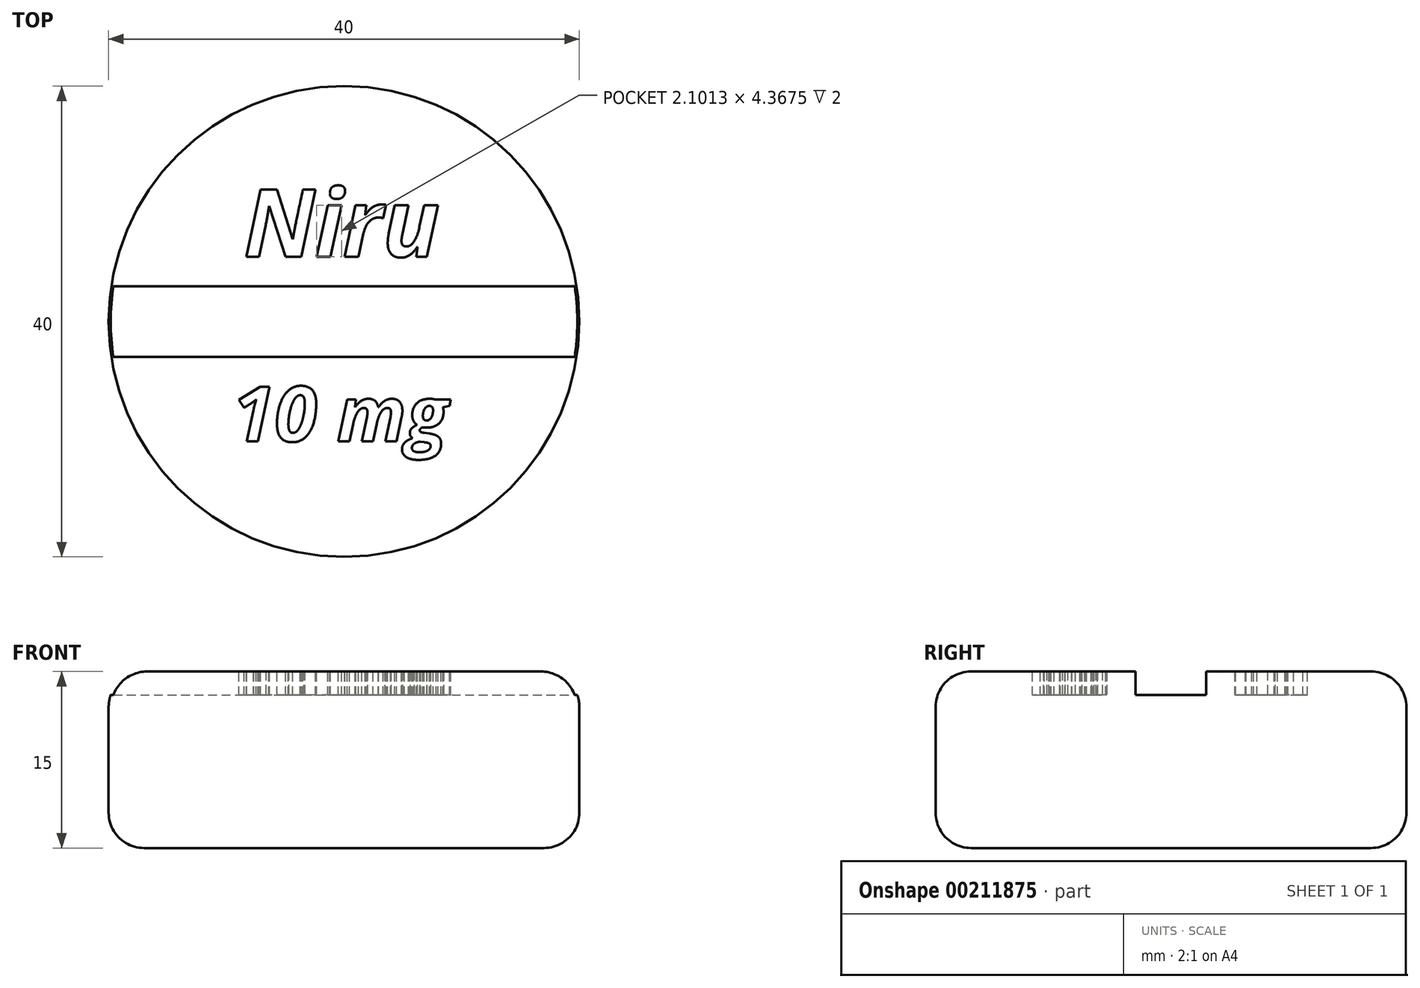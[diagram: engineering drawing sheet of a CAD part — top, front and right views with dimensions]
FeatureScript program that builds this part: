
annotation { "Feature Type Name" : "Feature", "Feature Type Description" : "" }
export const myFeature = defineFeature(function(context is Context, id is Id, definition is map)
    precondition{}
    {
        {
            var Q0;
            Q0=qCreatedBy(makeId("Top.planeOp"),FACE);
            var sketch = newSketch(context, id + "F0", { "sketchPlane" : qUnion([Q0])});
            skCircle(sketch, "E0", {"center": v(0, 0) * mm, "radius": 20 * mm});
            skSolve(sketch);
        }
        {
            var Q0;
            Q0=makeQuery(id+"F0.imprint","IMPRINT",FACE,{"disambiguationData":[TD([[makeQuery(id+"F0.imprint","IMPRINT",EDGE,{"derivedFrom":sQuery(id+"F0.wireOp",EDGE,"E0")}),1.0]])]});
            extrude(context, id + "F1", {"entities" : qUnion([Q0]), "depth" : 15 * mm});
        }
        {
            var Q0;
            Q0=makeQuery(id+"F1.opExtrude","CAP_EDGE",EDGE,{"disambiguationData":[OSD([sQuery(id+"F0.wireOp",EDGE,"E0")])],"isStart":false});
            var Q1;
            Q1=makeQuery(id+"F1.opExtrude","CAP_EDGE",EDGE,{"disambiguationData":[OSD([sQuery(id+"F0.wireOp",EDGE,"E0")])],"isStart":true});
            fillet(context, id + "F2", {"entities" : qUnion([Q0, Q1]), "radius" : 3 * mm, "tangentPropagation" : true, "allowEdgeOverflow" : false});
        }
        {
            var Q0;
            Q0=makeQuery(id+"F1.opExtrude","CAP_FACE",FACE,{"disambiguationData":[OSD([sQuery(id+"F0.wireOp",EDGE,"E0")])],"isStart":false});
            var sketch = newSketch(context, id + "F3", { "sketchPlane" : qUnion([Q0])});
            skLineSegment(sketch, "E1.bottom", {"start": v(-20, 3) * mm, "end": v(20, 3) * mm});
            skLineSegment(sketch, "E1.top", {"start": v(-20, -3) * mm, "end": v(20, -3) * mm});
            skLineSegment(sketch, "E1.left", {"start": v(-20, 3) * mm, "end": v(-20, -3) * mm});
            skLineSegment(sketch, "E1.right", {"start": v(20, 3) * mm, "end": v(20, -3) * mm});
            skSolve(sketch);
        }
        {
            var Q0;
            Q0 = qSketchRegion(id + "F3", true);
            extrude(context, id + "F4", {"entities" : qUnion([Q0]), "operationType" : NewBodyOperationType.REMOVE, "oppositeDirection" : true, "depth" : 2 * mm});
        }
        {
            var Q0;
            {var subQ0=sQuery(id+"F0.wireOp",EDGE,"E0");Q0=makeQuery(id+"F4.boolean.opBoolean","SPLIT",FACE,{"disambiguationData":[TD([makeQuery(id+"F4.opExtrude","SWEPT_FACE",FACE,{"disambiguationData":[OSD([sQuery(id+"F3.wireOp",EDGE,"E1.bottom")])]})])],"derivedFrom":makeQuery(id+"F1.opExtrude","CAP_FACE",FACE,{"disambiguationData":[OSD([subQ0])],"isStart":false})});}
            var sketch = newSketch(context, id + "F5", { "sketchPlane" : qUnion([Q0])});
            skText(sketch, "E2", { "text": "Niru", "fontName": "OpenSans-BoldItalic.ttf"});
            const initialGuessF5  = {"E2": [-0.0085, 0.0055, 1, 0, 0.00576]};
            skSetInitialGuess(sketch, initialGuessF5);
            skSolve(sketch);
        }
        {
            var Q0;
            Q0 = qSketchRegion(id + "F5", true);
            extrude(context, id + "F6", {"entities" : qUnion([Q0]), "operationType" : NewBodyOperationType.REMOVE, "oppositeDirection" : true, "depth" : 2 * mm});
        }
        {
            var Q0;
            {var subQ0=sQuery(id+"F0.wireOp",EDGE,"E0");Q0=makeQuery(id+"F4.boolean.opBoolean","SPLIT",FACE,{"disambiguationData":[TD([makeQuery(id+"F4.opExtrude","SWEPT_FACE",FACE,{"disambiguationData":[OSD([sQuery(id+"F3.wireOp",EDGE,"E1.top")])]})])],"derivedFrom":makeQuery(id+"F1.opExtrude","CAP_FACE",FACE,{"disambiguationData":[OSD([subQ0])],"isStart":false})});}
            var sketch = newSketch(context, id + "F7", { "sketchPlane" : qUnion([Q0])});
            skText(sketch, "E3", { "text": "10 mg", "fontName": "OpenSans-BoldItalic.ttf"});
            const initialGuessF7  = {"E3": [-0.0095, -0.0102, 1, 0, 0.0047]};
            skSetInitialGuess(sketch, initialGuessF7);
            skSolve(sketch);
        }
        {
            var Q0;
            Q0 = qSketchRegion(id + "F7", true);
            extrude(context, id + "F8", {"entities" : qUnion([Q0]), "operationType" : NewBodyOperationType.REMOVE, "oppositeDirection" : true, "depth" : 2 * mm});
        }
    });
